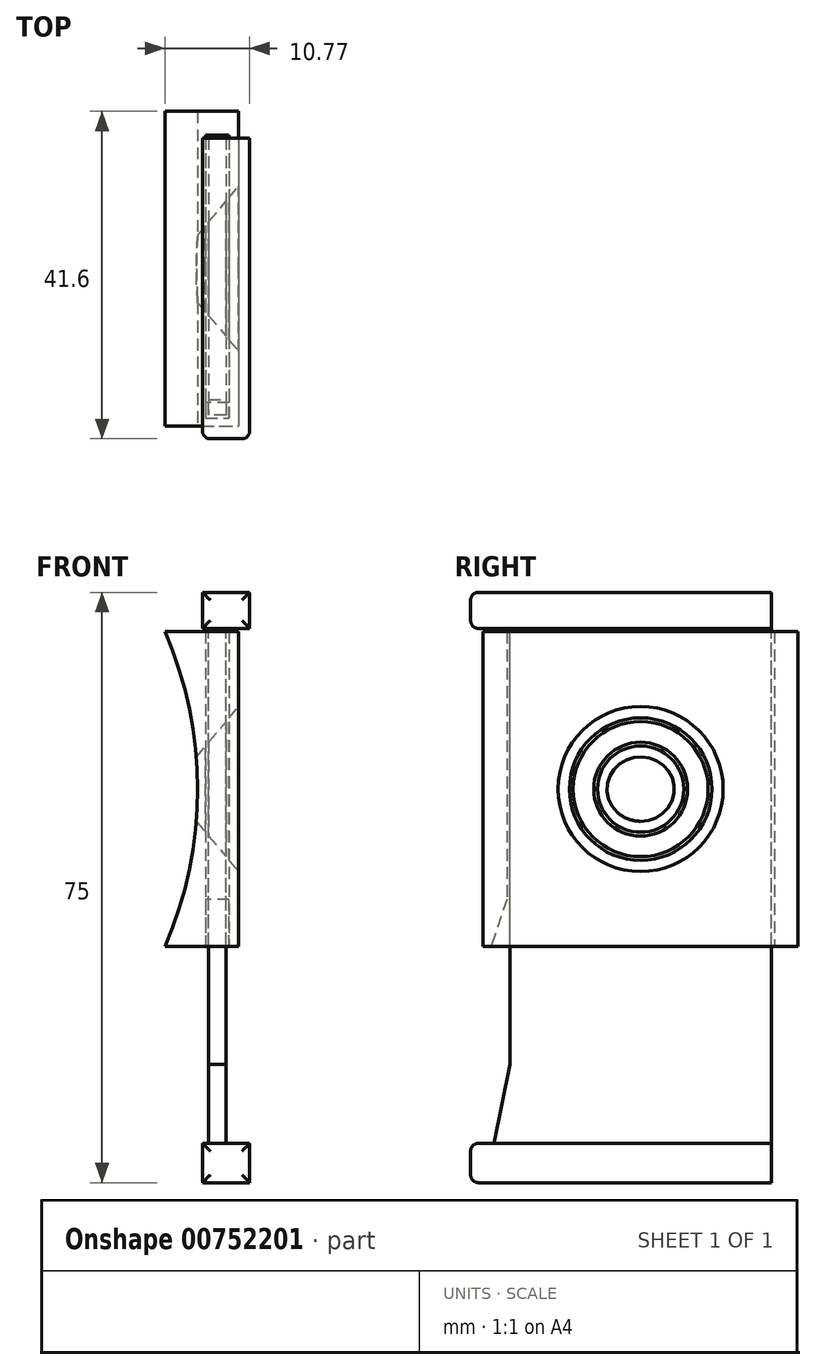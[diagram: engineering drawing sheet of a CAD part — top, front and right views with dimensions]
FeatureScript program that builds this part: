
annotation { "Feature Type Name" : "Feature", "Feature Type Description" : "" }
export const myFeature = defineFeature(function(context is Context, id is Id, definition is map)
    precondition{}
    {
        {
            var Q0;
            Q0=qCreatedBy(makeId("Top.planeOp"),FACE);
            var sketch = newSketch(context, id + "F0", { "sketchPlane" : qUnion([Q0])});
            skLineSegment(sketch, "E0.bottom", {"start": v(0, 20) * mm, "end": v(10, 20) * mm});
            skLineSegment(sketch, "E0.top", {"start": v(0, -20) * mm, "end": v(10, -20) * mm});
            skLineSegment(sketch, "E0.left", {"start": v(0, 20) * mm, "end": v(0, -20) * mm});
            skLineSegment(sketch, "E0.right", {"start": v(10, 20) * mm, "end": v(10, -20) * mm});
            skCircle(sketch, "E1", {"center": v(-41.2, 0) * mm, "radius": 50 * mm});
            skLineSegment(sketch, "E2.bottom", {"start": v(10, 20) * mm, "end": v(13, 20) * mm});
            skLineSegment(sketch, "E2.top", {"start": v(10, 17) * mm, "end": v(13, 17) * mm});
            skLineSegment(sketch, "E2.left", {"start": v(10, 20) * mm, "end": v(10, 17) * mm});
            skLineSegment(sketch, "E2.right", {"start": v(13, 20) * mm, "end": v(13, 17) * mm});
            skLineSegment(sketch, "E3.bottom", {"start": v(10, -20) * mm, "end": v(13, -20) * mm});
            skLineSegment(sketch, "E3.top", {"start": v(10, -17) * mm, "end": v(13, -17) * mm});
            skLineSegment(sketch, "E3.left", {"start": v(10, -20) * mm, "end": v(10, -17) * mm});
            skLineSegment(sketch, "E3.right", {"start": v(13, -20) * mm, "end": v(13, -17) * mm});
            skLineSegment(sketch, "E4.bottom", {"start": v(13, 20) * mm, "end": v(14.2, 20) * mm});
            skLineSegment(sketch, "E4.top", {"start": v(13, -20) * mm, "end": v(14.2, -20) * mm});
            skLineSegment(sketch, "E4.left", {"start": v(13, 20) * mm, "end": v(13, -20) * mm});
            skLineSegment(sketch, "E4.right", {"start": v(14.2, 20) * mm, "end": v(14.2, -20) * mm});
            skLineSegment(sketch, "E5.left", {"start": v(13, -20) * mm, "end": v(13, -20) * mm});
            skLineSegment(sketch, "E5.right", {"start": v(14.2, -20) * mm, "end": v(14.2, -20) * mm});
            skSolve(sketch);
        }
        {
            var Q0;
            Q0=makeQuery(id+"F0.imprint","IMPRINT",FACE,{"disambiguationData":[TD([[makeQuery(id+"F0.imprint","IMPRINT",EDGE,{"derivedFrom":sQuery(id+"F0.wireOp",EDGE,"E0.right")}),-1.0]])]});
            var Q1;
            {var subQ0=sQuery(id+"F0.wireOp",EDGE,"E2.bottom");Q1=makeQuery(id+"F0.imprint","IMPRINT",FACE,{"disambiguationData":[TD([[makeQuery(id+"F0.imprint","IMPRINT",EDGE,{"derivedFrom":subQ0}),-1.0]])]});}
            var Q2;
            {var subQ4=sQuery(id+"F0.wireOp",EDGE,"E4.bottom");Q2=makeQuery(id+"F0.imprint","IMPRINT",FACE,{"disambiguationData":[TD([[makeQuery(id+"F0.imprint","IMPRINT",EDGE,{"derivedFrom":subQ4}),-1.0]])]});}
            var Q3;
            {var subQ0=sQuery(id+"F0.wireOp",EDGE,"E3.bottom");Q3=makeQuery(id+"F0.imprint","IMPRINT",FACE,{"disambiguationData":[TD([[makeQuery(id+"F0.imprint","IMPRINT",EDGE,{"derivedFrom":subQ0}),1.0]])]});}
            var Q4;
            {var subQ0=sQuery(id+"F0.wireOp",EDGE,"E0.left");Q4=makeQuery(id+"F0.imprint","IMPRINT",FACE,{"disambiguationData":[TD([[makeQuery(id+"F0.imprint","IMPRINT",EDGE,{"derivedFrom":subQ0}),1.0]])]});}
            extrude(context, id + "F1", {"entities" : qUnion([Q0, Q1, Q2, Q3, Q4]), "endBound" : BoundingType.SYMMETRIC, "depth" : 40 * mm, "offsetDistance" : 25 * mm});
        }
        {
            var Q0;
            Q0=qCreatedBy(makeId("Front.planeOp"),FACE);
            var sketch = newSketch(context, id + "F2", { "sketchPlane" : qUnion([Q0])});
            skCircle(sketch, "E6", {"center": v(-41, 0) * mm, "radius": 50 * mm});
            skSolve(sketch);
        }
        {
            var Q0;
            Q0 = qSketchRegion(id + "F2", true);
            extrude(context, id + "F3", {"entities" : qUnion([Q0]), "operationType" : NewBodyOperationType.REMOVE, "endBound" : BoundingType.SYMMETRIC, "oppositeDirection" : true, "depth" : 50 * mm, "offsetDistance" : 25 * mm});
        }
        {
            var Q0;
            Q0=makeQuery(id+"F1.opExtrude","CAP_FACE",FACE,{"disambiguationData":[OSD([sQuery(id+"F0.wireOp",EDGE,"E0.bottom"),sQuery(id+"F0.wireOp",EDGE,"E0.top"),sQuery(id+"F0.wireOp",EDGE,"E0.left"),sQuery(id+"F0.wireOp",EDGE,"E0.right"),sQuery(id+"F0.wireOp",EDGE,"E2.bottom"),sQuery(id+"F0.wireOp",EDGE,"E2.top"),sQuery(id+"F0.wireOp",EDGE,"E3.bottom"),sQuery(id+"F0.wireOp",EDGE,"E3.top"),sQuery(id+"F0.wireOp",EDGE,"E4.bottom"),sQuery(id+"F0.wireOp",EDGE,"E4.left"),sQuery(id+"F0.wireOp",EDGE,"E4.right"),sQuery(id+"F0.wireOp",EDGE,"E4.top")])],"isStart":false});
            var sketch = newSketch(context, id + "F4", { "sketchPlane" : qUnion([Q0])});
            skLineSegment(sketch, "E7.bottom", {"start": v(10.4, 16.6) * mm, "end": v(12.6, 16.6) * mm});
            skLineSegment(sketch, "E7.top", {"start": v(10.4, -16.6) * mm, "end": v(12.6, -16.6) * mm});
            skLineSegment(sketch, "E7.left", {"start": v(10.4, 16.6) * mm, "end": v(10.4, -16.6) * mm});
            skLineSegment(sketch, "E7.right", {"start": v(12.6, 16.6) * mm, "end": v(12.6, -16.6) * mm});
            skSolve(sketch);
        }
        {
            var Q0;
            Q0=makeQuery(id+"F4.imprint","IMPRINT",FACE,{"disambiguationData":[TD([[makeQuery(id+"F4.imprint","IMPRINT",EDGE,{"derivedFrom":sQuery(id+"F4.wireOp",EDGE,"E7.bottom")}),-1.0]])]});
            extrude(context, id + "F5", {"entities" : qUnion([Q0]), "oppositeDirection" : true, "depth" : 70 * mm, "offsetDistance" : 25 * mm, "hasSecondDirection" : true, "secondDirectionOppositeDirection" : false, "secondDirectionDepth" : 5 * mm});
        }
        {
            var Q0;
            Q0=qCreatedBy(makeId("Right.planeOp"),FACE);
            cPlane(context, id + "F6", {"entities" : qUnion([Q0]), "cplaneType" : CPlaneType.OFFSET, "offset" : 7.92 * mm, "width" : 150 * mm, "height" : 150 * mm});
        }
        {
            var Q0;
            Q0=qCreatedBy(id+"F6.planeOp",FACE);
            var sketch = newSketch(context, id + "F7", { "sketchPlane" : qUnion([Q0])});
            skCircle(sketch, "E8", {"center": v(0, 0) * mm, "radius": 3 * mm});
            skSolve(sketch);
        }
        {
            var Q0;
            Q0 = qSketchRegion(id + "F7", true);
            extrude(context, id + "F8", {"entities" : qUnion([Q0]), "operationType" : NewBodyOperationType.REMOVE, "depth" : 25 * mm, "offsetDistance" : 25 * mm, "hasDraft" : true, "draftAngle" : 50 * degree});
        }
        {
            var Q0;
            Q0=makeQuery(id+"F5.opExtrude","SWEPT_FACE",FACE,{"disambiguationData":[OSD([sQuery(id+"F4.wireOp",EDGE,"E7.right")])]});
            var sketch = newSketch(context, id + "F9", { "sketchPlane" : qUnion([Q0])});
            skLineSegment(sketch, "E9.bottom", {"start": v(16.6, 25) * mm, "end": v(-21.6, 25) * mm});
            skLineSegment(sketch, "E9.top", {"start": v(16.6, 20.4) * mm, "end": v(-21.6, 20.4) * mm});
            skLineSegment(sketch, "E9.left", {"start": v(16.6, 25) * mm, "end": v(16.6, 20.4) * mm});
            skLineSegment(sketch, "E9.right", {"start": v(-21.6, 25) * mm, "end": v(-21.6, 20.4) * mm});
            skLineSegment(sketch, "E10.bottom", {"start": v(16.6, -50) * mm, "end": v(-21.6, -50) * mm});
            skLineSegment(sketch, "E10.top", {"start": v(16.6, -45) * mm, "end": v(-21.6, -45) * mm});
            skLineSegment(sketch, "E10.left", {"start": v(16.6, -50) * mm, "end": v(16.6, -45) * mm});
            skLineSegment(sketch, "E10.right", {"start": v(-21.6, -50) * mm, "end": v(-21.6, -45) * mm});
            skSolve(sketch);
        }
        {
            var Q0;
            Q0 = qSketchRegion(id + "F9", true);
            extrude(context, id + "F10", {"entities" : qUnion([Q0]), "operationType" : NewBodyOperationType.ADD, "depth" : 3 * mm, "offsetDistance" : 25 * mm, "hasSecondDirection" : true, "secondDirectionOppositeDirection" : true, "secondDirectionDepth" : 3 * mm});
        }
        {
            var Q0;
            Q0=makeQuery(id+"F10.opExtrude","SWEPT_FACE",FACE,{"disambiguationData":[OSD([sQuery(id+"F9.wireOp",EDGE,"E10.right")])]});
            var Q1;
            Q1=makeQuery(id+"F10.opExtrude","SWEPT_FACE",FACE,{"disambiguationData":[OSD([sQuery(id+"F9.wireOp",EDGE,"E9.right")])]});
            fillet(context, id + "F11", {"entities" : qUnion([Q0, Q1]), "radius" : 1 * mm, "tangentPropagation" : true, "allowEdgeOverflow" : false});
        }
        {
            var Q0;
            Q0=makeQuery(id+"F10.boolean.opBoolean","INTERSECT",EDGE,{"derivedFrom":[makeQuery(id+"F5.opExtrude","SWEPT_FACE",FACE,{"disambiguationData":[OSD([sQuery(id+"F4.wireOp",EDGE,"E7.top")])]}),makeQuery(id+"F10.opExtrude","SWEPT_FACE",FACE,{"disambiguationData":[OSD([sQuery(id+"F9.wireOp",EDGE,"E10.top")])]})]});
            chamfer(context, id + "F12", {"entities" : qUnion([Q0]), "chamferType" : ChamferType.TWO_OFFSETS, "width1" : 10 * mm, "oppositeDirection" : false, "width2" : 2 * mm, "tangentPropagation" : true});
        }
        {
            var Q0;
            Q0=makeQuery(id+"F1.opExtrude","CAP_EDGE",EDGE,{"disambiguationData":[OSD([sQuery(id+"F0.wireOp",EDGE,"E3.top")])],"isStart":true});
            chamfer(context, id + "F13", {"entities" : qUnion([Q0]), "chamferType" : ChamferType.TWO_OFFSETS, "width1" : 2 * mm, "oppositeDirection" : false, "width2" : 6 * mm, "tangentPropagation" : true});
        }
    });
